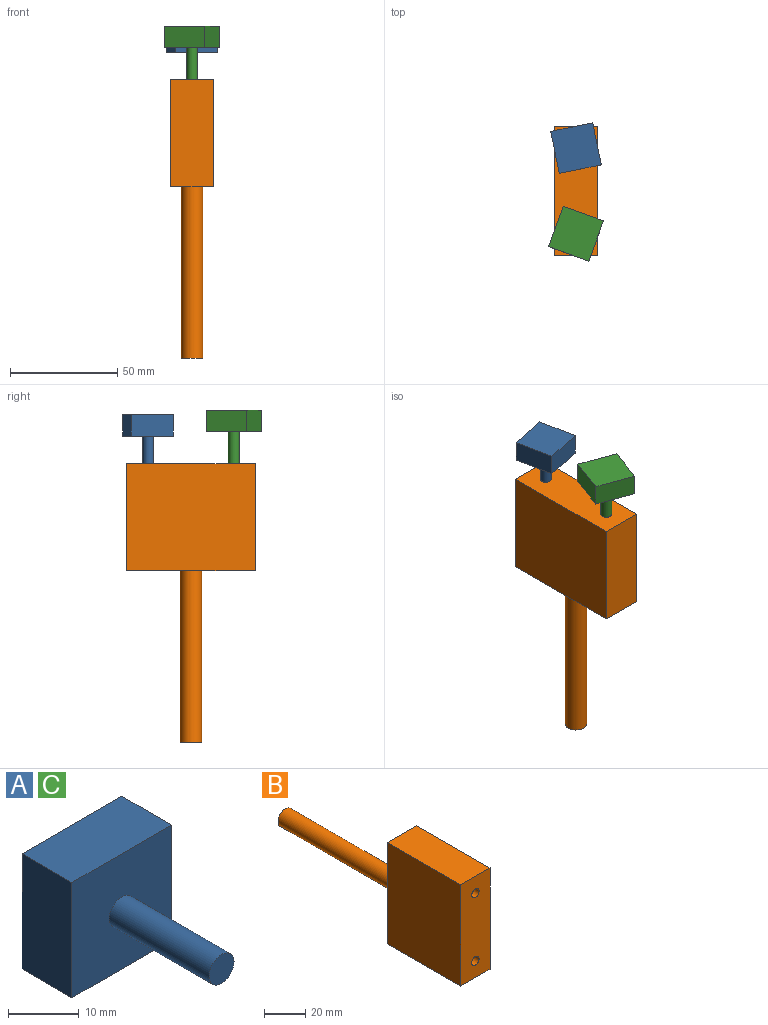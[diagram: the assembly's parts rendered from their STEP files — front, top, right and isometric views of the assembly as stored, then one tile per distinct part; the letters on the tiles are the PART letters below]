
ASSEMBLY  parts=3 mates=2
PART A: 8 faces, bbox 20x30x20 mm
  f0: plane 20x10mm, normal (-1,0,0), area 200mm2, adj f1,f3,f4,f7
  f1: plane 20x20mm, normal (0,-1,0), area 380.4mm2, adj f0,f2,f3,f4,f5
  f2: plane 20x10mm, normal (1,0,0), area 200mm2, adj f1,f3,f4,f7
  f3: plane 20x10mm, normal (0,0,1), area 200mm2, adj f0,f1,f2,f7
  f4: plane 20x10mm, normal (0,0,-1), area 200mm2, adj f0,f1,f2,f7
  f5: cylinder r=2.5mm len=20mm, axis (0,1,0), area 314.2mm2, adj f1,f6
  f6: plane 5x5mm, normal (0,-1,0), area 19.6mm2, adj f5
  f7: plane 20x20mm, normal (0,1,0), area 400mm2, adj f0,f2,f3,f4
PART B: 12 faces, bbox 20x130x60 mm
  f0: plane 60x50mm, normal (-1,0,0), area 3000mm2, adj f1,f3,f4,f5
  f1: plane 60x20mm, normal (0,-1,0), area 1160.7mm2, adj f0,f2,f4,f5,f6,f8
  f2: plane 60x50mm, normal (1,0,0), area 3000mm2, adj f1,f3,f4,f5
  f3: plane 60x20mm, normal (0,1,0), area 1121.5mm2, adj f0,f2,f4,f5,f10
  f4: plane 50x20mm, normal (0,0,1), area 1000mm2, adj f0,f1,f2,f3
  f5: plane 50x20mm, normal (0,0,-1), area 1000mm2, adj f0,f1,f2,f3
  f6: cylinder r=2.5mm len=20mm, axis (0,-1,0), area 314.2mm2, adj f1,f7
  f7: plane 5x5mm, normal (0,-1,0), area 19.6mm2, adj f6
  f8: cylinder r=2.5mm len=20mm, axis (0,-1,0), area 314.2mm2, adj f1,f9
  f9: plane 5x5mm, normal (0,-1,0), area 19.6mm2, adj f8
  f10: cylinder r=5mm len=80mm, axis (0,-1,0), area 2513.3mm2, adj f3,f11
  f11: plane 10x10mm, normal (0,1,0), area 78.5mm2, adj f10
PART C: same geometry as A
PLACE A rot(axis=(0.5,0.61,0.61),126.9deg) t=(-48.98,19.95,102.4)mm
PLACE B rot(axis=(-1,0,0),90deg) t=(0,-19.99,39.45)mm fixed
PLACE C rot(axis=(0.71,0.5,0.5),109.2deg) t=(-46.99,7.08,104.59)mm
MATE cylindrical A.f5 <-> B.f8  axis (0,0,-1) through (0,30.01,57.4)mm
MATE cylindrical C.f5 <-> B.f6  axis (0,0,-1) through (0,-9.99,59.59)mm
